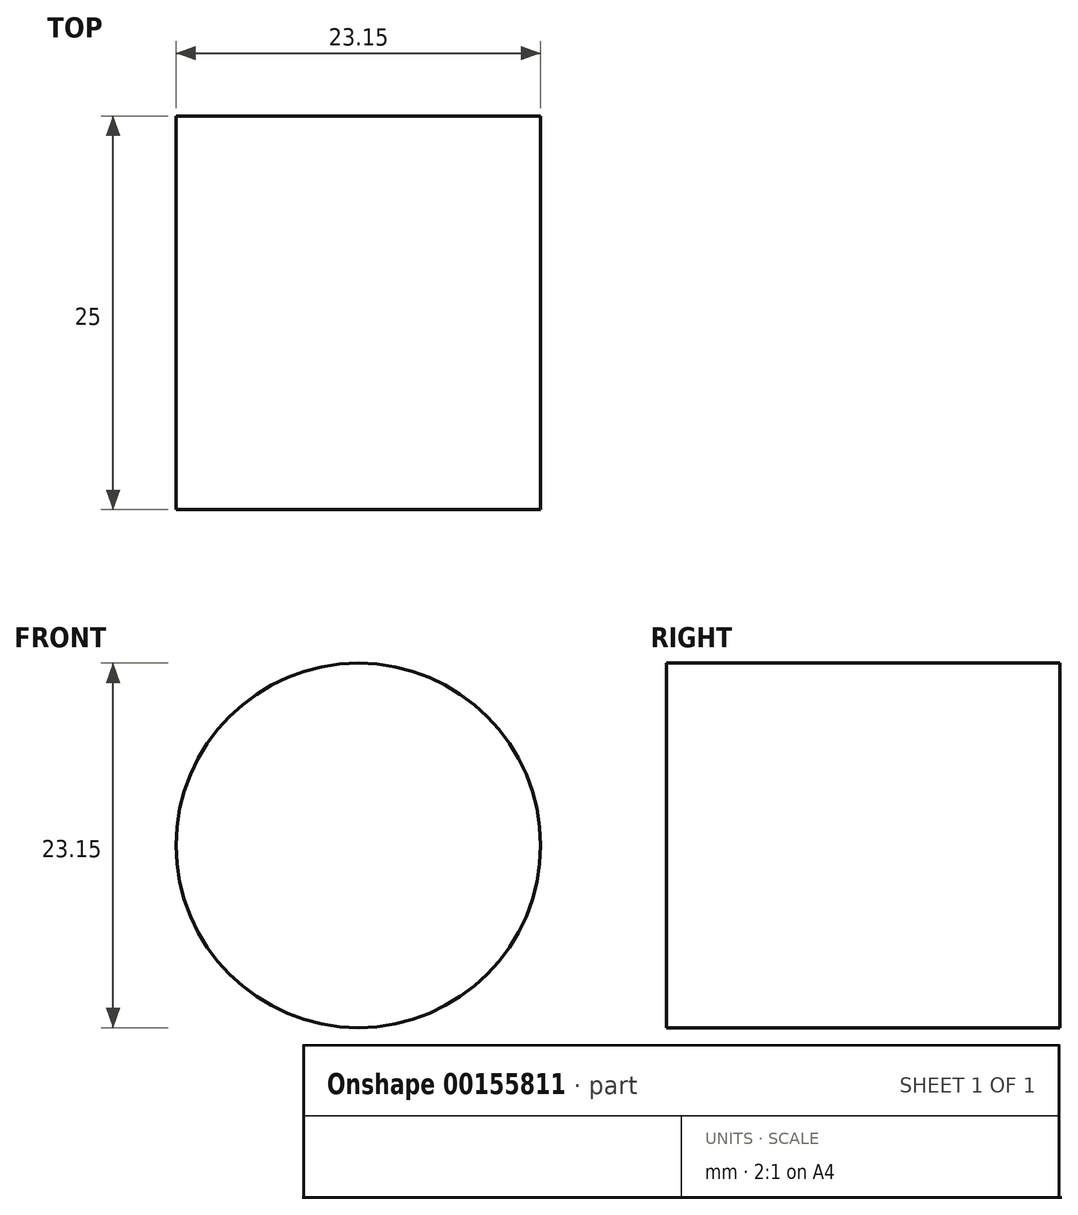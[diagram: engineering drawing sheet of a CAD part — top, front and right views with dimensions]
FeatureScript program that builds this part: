
annotation { "Feature Type Name" : "Feature", "Feature Type Description" : "" }
export const myFeature = defineFeature(function(context is Context, id is Id, definition is map)
    precondition{}
    {
        {
            var Q0;
            Q0=qCreatedBy(makeId("Front.planeOp"),FACE);
            var sketch = newSketch(context, id + "F0", { "sketchPlane" : qUnion([Q0])});
            skCircle(sketch, "E0", {"center": v(-55.96, 40.82) * mm, "radius": 11.57 * mm});
            skSolve(sketch);
        }
        {
            var Q0;
            Q0=makeQuery(id+"F0.imprint","IMPRINT",FACE,{"disambiguationData":[TD([[makeQuery(id+"F0.imprint","IMPRINT",EDGE,{"derivedFrom":sQuery(id+"F0.wireOp",EDGE,"E0")}),1.0]])]});
            extrude(context, id + "F1", {"entities" : qUnion([Q0]), "depth" : 25 * mm});
        }
    });
